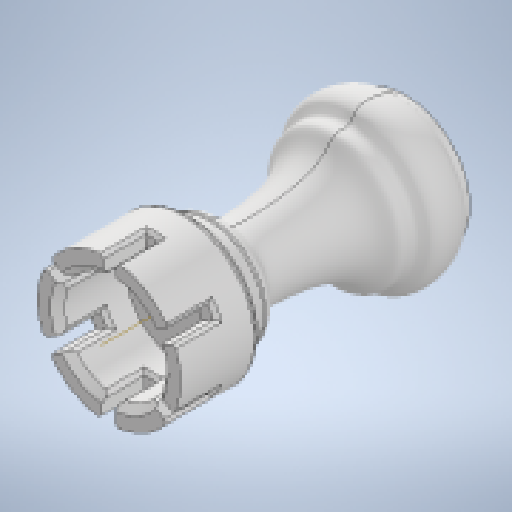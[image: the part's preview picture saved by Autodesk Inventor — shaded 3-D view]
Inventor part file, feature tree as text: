
AUTODESK INVENTOR PART (.ipt)
format: ipt  version: 2024.1 (Build 281209000, 209)  size: 657,408 bytes
history: native  units: mm
features: sketch x5, extrude x4, fillet x3, chamfer x3, other x1, revolve x1, pattern_circular x1, projected_geometry x1
ambient origin geometry x8: Origin, YZ Plane, XZ Plane, XY Plane, X Axis, Y Axis, Z Axis, Center Point
bodies: Solid1 (feature_tree)
feature tree (19):
  extrude  "Extrusion1"  Depth=10.0mm TaperAngle=0.0deg
  other  "Work Axis1"
  extrude  "Extrusion2"  Depth=14.3mm
  revolve  "Revolution1"  [1 undecoded]
  extrude  "Extrusion12"  Depth=6.2mm
  extrude  "Extrusion13"  Depth=33.1mm
  pattern_circular  "Circular Pattern6"  [2 undecoded]
  fillet  "Fillet9"  Radius=0.2mm
  fillet  "Fillet10"  Radius=1.8mm
  fillet  "Fillet11"  Radius=11.5mm
  chamfer  "Chamfer7"  Distance=7.65mm
  chamfer  "Chamfer8"  Distance=1.4mm
  chamfer  "Chamfer9"  Distance=0.7mm
  sketch  "Sketch1"  dims[d0=10.0mm d1=3.0mm d2=0.0mm]
  sketch  "Sketch2"  dims[d5=360.0deg d6=14.3mm]
  sketch  "Sketch3"  dims[d7=3.0mm d8=0.0mm d135=0.8mm]
  projected_geometry  "Projected Loop1"
  sketch  "Sketch18"  dims[d146=22.0mm d147=6.2mm]
  sketch  "Sketch19"  dims[d151=8.0mm d152=33.1mm d153=8.4mm d154=0.2mm d155=1.8mm d156=11.5mm d157=7.65mm d158=0.0mm d159=1.4mm d160=0.7mm d161=4.73mm d162=0.0mm d163=30.0mm d164=360.0deg d166=0.5mm d167=0.5mm d168=0.2mm d169=0.4mm d170=2.0mm d171=45.0deg d172=0.4mm d173=2.0mm d174=45.0deg d175=0.8mm d176=2.0mm d177=45.0deg d98=0.0mm d99=0.0mm d100=0.0mm d101=0.0mm]
note: 3 required parameter values undecoded (feature->parameter linkage not recoverable at this tier; creation-order binding heuristic only, values carry confidence <= 0.55)